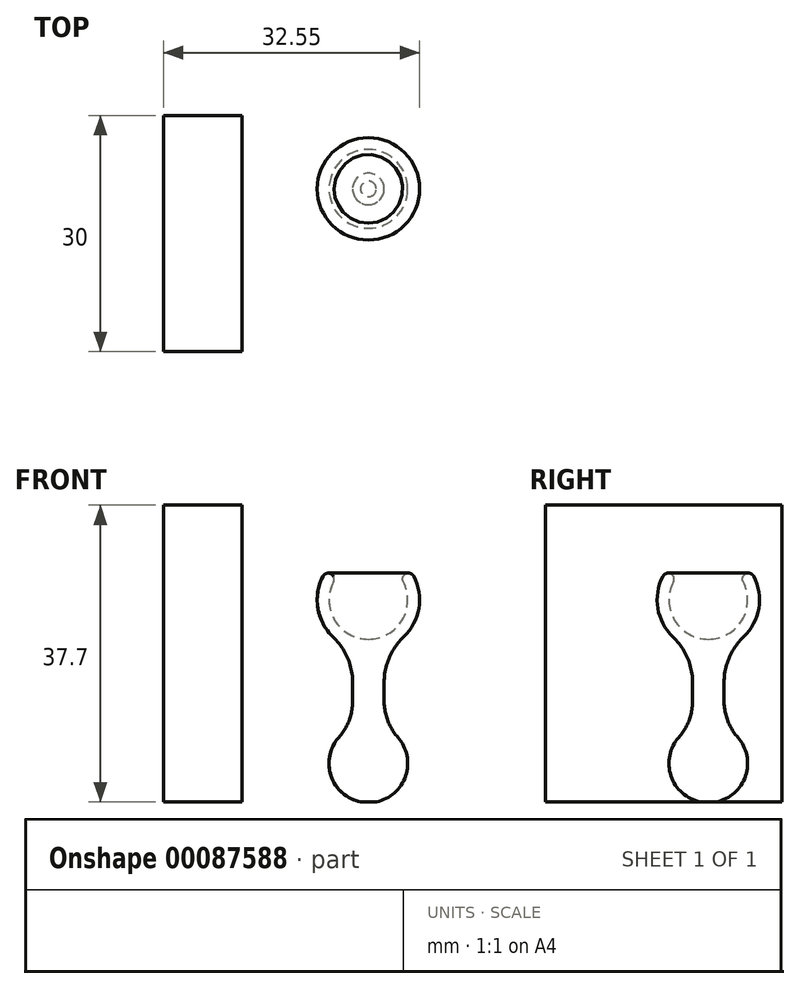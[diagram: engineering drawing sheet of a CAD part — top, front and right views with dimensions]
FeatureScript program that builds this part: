
annotation { "Feature Type Name" : "Feature", "Feature Type Description" : "" }
export const myFeature = defineFeature(function(context is Context, id is Id, definition is map)
    precondition{}
    {
        {
            var Q0;
            Q0=qCreatedBy(makeId("Front.planeOp"),FACE);
            var sketch = newSketch(context, id + "F0", { "sketchPlane" : qUnion([Q0])});
            skArc(sketch, "E0", {"start": v(-4.44, 2.3) * mm, "mid": v(-4.27, -2.6) * mm, "end": v(0, -5) * mm});
            skArc(sketch, "E1", {"start": v(-5.77, 3) * mm, "mid": v(-6.01, -2.47) * mm, "end": v(-2, -6.18) * mm});
            skLineSegment(sketch, "E2", {"start": v(-4.44, 2.3) * mm, "end": v(-5.77, 3) * mm, "construction": true});
            skLineSegment(sketch, "E3", {"start": v(0, -5) * mm, "end": v(0, -13.57) * mm, "construction": true});
            skArc(sketch, "E4", {"start": v(-4.44, 2.3) * mm, "mid": v(-4.75, 3.32) * mm, "end": v(-5.77, 3) * mm});
            skPoint(sketch, "E5.endSnap0", {"position": v(0, -6.78) * mm});
            skLineSegment(sketch, "E6.trimOffspring", {"start": v(0, -5) * mm, "end": v(0, -6.5) * mm});
            skLineSegment(sketch, "E7", {"start": v(-2, -6.18) * mm, "end": v(-2, -16.18) * mm});
            skLineSegment(sketch, "E8", {"start": v(0, -15) * mm, "end": v(0, -6.5) * mm});
            skArc(sketch, "E9", {"start": v(-2, -16.18) * mm, "mid": v(-4.97, -21.3) * mm, "end": v(-1, -25.67) * mm});
            skLineSegment(sketch, "E10", {"start": v(0, -15) * mm, "end": v(0, -25.77) * mm});
            skLineSegment(sketch, "E11", {"start": v(-1, -25.67) * mm, "end": v(0, -25.67) * mm});
            skCircle(sketch, "E12", {"center": v(0, 5.31) * mm, "radius": 5 * mm, "construction": true});
            skLineSegment(sketch, "E13", {"start": v(-5, 12.12) * mm, "end": v(-5, -24.33) * mm, "construction": true});
            skCircle(sketch, "E14", {"center": v(0, 0) * mm, "radius": 5 * mm, "construction": true});
            skLineSegment(sketch, "E15", {"start": v(-4.44, 2.3) * mm, "end": v(-4.44, -8.55) * mm, "construction": true});
            skSolve(sketch);
        }
        {
            var Q0;
            Q0=makeQuery(id+"F0.imprint","IMPRINT",FACE,{"disambiguationData":[TD([[makeQuery(id+"F0.imprint","IMPRINT",EDGE,{"derivedFrom":sQuery(id+"F0.wireOp",EDGE,"E0")}),-1.0]])]});
            var Q1;
            Q1=sQuery(id+"F0.wireOp",EDGE,"E8");
            revolve(context, id + "F1", {"entities" : qUnion([Q0]), "axis" : qUnion([Q1]), "revolveType" : RevolveType.FULL});
        }
        {
            var Q0;
            Q0=makeQuery(id+"F1.opRevolve","SWEPT_EDGE",EDGE,{"disambiguationData":[OSD([sQuery(id+"F0.wireOp",EDGE,"E1"),sQuery(id+"F0.wireOp",EDGE,"E7")])]});
            fillet(context, id + "F2", {"entities" : qUnion([Q0]), "radius" : 8 * mm, "tangentPropagation" : true, "allowEdgeOverflow" : false});
        }
        {
            var Q0;
            Q0=makeQuery(id+"F1.opRevolve","SWEPT_EDGE",EDGE,{"disambiguationData":[OSD([sQuery(id+"F0.wireOp",EDGE,"E7"),sQuery(id+"F0.wireOp",EDGE,"ywg5SL3T-TYOw-sGt6-3Rzi-PARAZnVLxAsf")])]});
            fillet(context, id + "F3", {"entities" : qUnion([Q0]), "radius" : 7 * mm, "tangentPropagation" : true, "allowEdgeOverflow" : false});
        }
        {
            var Q0;
            Q0=makeQuery(id+"F1.opRevolve","SWEPT_FACE",FACE,{"disambiguationData":[OSD([sQuery(id+"F0.wireOp",EDGE,"E11")])]});
            var sketch = newSketch(context, id + "F4", { "sketchPlane" : qUnion([Q0])});
            skLineSegment(sketch, "E16.bottom", {"start": v(-26.05, -9.32) * mm, "end": v(-16.05, -9.32) * mm});
            skLineSegment(sketch, "E16.top", {"start": v(-26.05, 20.68) * mm, "end": v(-16.05, 20.68) * mm});
            skLineSegment(sketch, "E16.left", {"start": v(-26.05, -9.32) * mm, "end": v(-26.05, 20.68) * mm});
            skLineSegment(sketch, "E16.right", {"start": v(-16.05, -9.32) * mm, "end": v(-16.05, 20.68) * mm});
            skSolve(sketch);
        }
        {
            var Q0;
            Q0=makeQuery(id+"F4.imprint","IMPRINT",FACE,{"disambiguationData":[TD([[makeQuery(id+"F4.imprint","IMPRINT",EDGE,{"derivedFrom":sQuery(id+"F4.wireOp",EDGE,"E16.bottom")}),1.0]])]});
            extrude(context, id + "F5", {"entities" : qUnion([Q0]), "oppositeDirection" : true, "depth" : 37.7 * mm});
        }
    });
